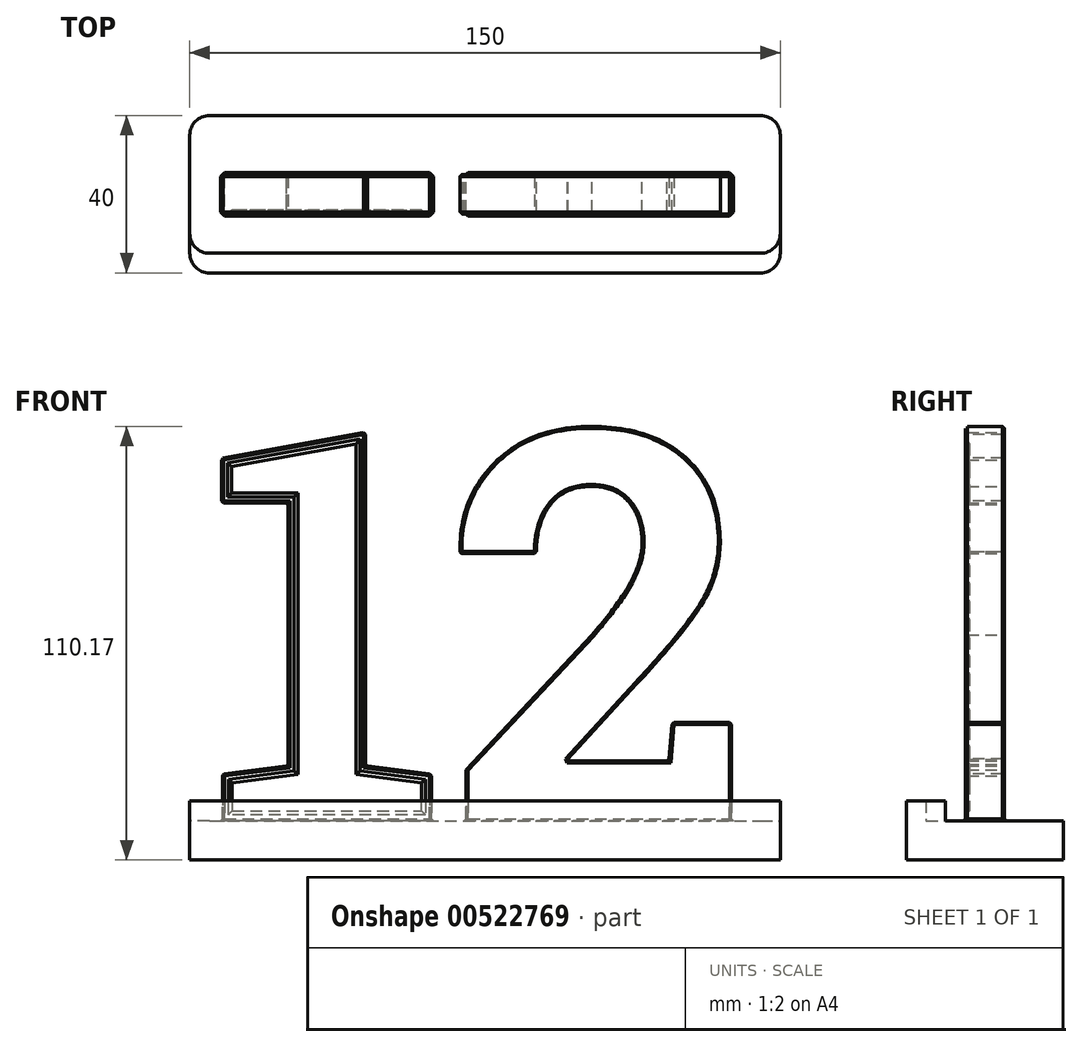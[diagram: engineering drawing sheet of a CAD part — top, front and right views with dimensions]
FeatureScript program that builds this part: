
annotation { "Feature Type Name" : "Feature", "Feature Type Description" : "" }
export const myFeature = defineFeature(function(context is Context, id is Id, definition is map)
    precondition{}
    {
        {
            var Q0;
            Q0=qCreatedBy(makeId("Front.planeOp"),FACE);
            var sketch = newSketch(context, id + "F0", { "sketchPlane" : qUnion([Q0])});
            skText(sketch, "E0", { "text": "12", "fontName": "RobotoSlab-Bold.ttf"});
            const initialGuessF0  = {"E0": [-0.07112, 0, 1, 0, 0.1]};
            skSetInitialGuess(sketch, initialGuessF0);
            skSolve(sketch);
        }
        {
            var Q0;
            Q0=makeQuery(id+"F0.imprint","IMPRINT",FACE,{"disambiguationData":[TD([[makeQuery(id+"F0.imprint","IMPRINT",EDGE,{"derivedFrom":sQuery(id+"F0.wireOp",EDGE,"E0.sketch_text.stroke-0")}),-1.0]])]});
            var Q1;
            Q1=makeQuery(id+"F0.imprint","IMPRINT",FACE,{"disambiguationData":[TD([[makeQuery(id+"F0.imprint","IMPRINT",EDGE,{"derivedFrom":sQuery(id+"F0.wireOp",EDGE,"E0.sketch_text.stroke-10")}),-1.0]])]});
            extrude(context, id + "F1", {"entities" : qUnion([Q0, Q1]), "depth" : 5 * mm, "offsetDistance" : 25 * mm, "hasSecondDirection" : true, "secondDirectionOppositeDirection" : true, "secondDirectionDepth" : 5 * mm});
        }
        {
            var Q0;
            Q0=qCreatedBy(makeId("Front.planeOp"),FACE);
            var sketch = newSketch(context, id + "F2", { "sketchPlane" : qUnion([Q0])});
            skLineSegment(sketch, "E1.bottom", {"start": v(-75, -10) * mm, "end": v(75, -10) * mm});
            skLineSegment(sketch, "E1.top", {"start": v(-75, 0) * mm, "end": v(75, 0) * mm});
            skLineSegment(sketch, "E1.left", {"start": v(-75, -10) * mm, "end": v(-75, 0) * mm});
            skLineSegment(sketch, "E1.right", {"start": v(75, -10) * mm, "end": v(75, 0) * mm});
            skSolve(sketch);
        }
        {
            var Q0;
            Q0=makeQuery(id+"F2.imprint","IMPRINT",FACE,{"disambiguationData":[TD([[makeQuery(id+"F2.imprint","IMPRINT",EDGE,{"derivedFrom":sQuery(id+"F2.wireOp",EDGE,"E1.bottom")}),1.0]])]});
            extrude(context, id + "F3", {"entities" : qUnion([Q0]), "operationType" : NewBodyOperationType.ADD, "depth" : 20 * mm, "offsetDistance" : 25 * mm, "hasSecondDirection" : true, "secondDirectionOppositeDirection" : true, "secondDirectionDepth" : 20 * mm});
        }
        {
            var Q0;
            Q0=makeQuery(id+"F1.opExtrude","CAP_FACE",FACE,{"disambiguationData":[OSD([sQuery(id+"F0.wireOp",EDGE,"E0.sketch_text.stroke-0"),sQuery(id+"F0.wireOp",EDGE,"E0.sketch_text.stroke-1"),sQuery(id+"F0.wireOp",EDGE,"E0.sketch_text.stroke-2"),sQuery(id+"F0.wireOp",EDGE,"E0.sketch_text.stroke-3"),sQuery(id+"F0.wireOp",EDGE,"E0.sketch_text.stroke-4"),sQuery(id+"F0.wireOp",EDGE,"E0.sketch_text.stroke-5"),sQuery(id+"F0.wireOp",EDGE,"E0.sketch_text.stroke-6"),sQuery(id+"F0.wireOp",EDGE,"E0.sketch_text.stroke-7"),sQuery(id+"F0.wireOp",EDGE,"E0.sketch_text.stroke-8"),sQuery(id+"F0.wireOp",EDGE,"E0.sketch_text.stroke-9")])],"isStart":false});
            var sketch = newSketch(context, id + "F4", { "sketchPlane" : qUnion([Q0])});
            skLineSegment(sketch, "E2.0", {"start": v(-48.02, 12.14) * mm, "end": v(-64.71, 10.1) * mm});
            skLineSegment(sketch, "E2.1", {"start": v(-48.02, 82.77) * mm, "end": v(-48.02, 12.14) * mm});
            skLineSegment(sketch, "E2.2", {"start": v(-64.71, 10.1) * mm, "end": v(-64.71, 2) * mm});
            skLineSegment(sketch, "E2.3", {"start": v(-64.9, 82.77) * mm, "end": v(-48.02, 82.77) * mm});
            skLineSegment(sketch, "E2.4", {"start": v(-64.9, 90.43) * mm, "end": v(-64.9, 82.77) * mm});
            skLineSegment(sketch, "E2.5", {"start": v(-32.3, 96.35) * mm, "end": v(-64.9, 90.43) * mm});
            skLineSegment(sketch, "E2.6", {"start": v(-64.71, 2) * mm, "end": v(-15.6, 2) * mm});
            skLineSegment(sketch, "E2.7", {"start": v(-15.6, 2) * mm, "end": v(-15.6, 10.1) * mm});
            skLineSegment(sketch, "E2.8", {"start": v(-15.6, 10.1) * mm, "end": v(-32.3, 12.14) * mm});
            skLineSegment(sketch, "E2.9", {"start": v(-32.3, 12.14) * mm, "end": v(-32.3, 96.35) * mm});
            skFitSpline(sketch, "E3.0", {"points": [v(15.01, 81.48) * mm, v(13.83, 79.93) * mm, v(12, 76.41) * mm, v(11.24, 72.17) * mm, v(11.1, 69.88) * mm]});
            skFitSpline(sketch, "E3.1", {"points": [v(27.02, 86.92) * mm, v(25.76, 86.92) * mm, v(23.36, 86.7) * mm, v(20.1, 85.7) * mm, v(17.26, 83.98) * mm, v(15.7, 82.38) * mm, v(15.01, 81.48) * mm]});
            skFitSpline(sketch, "E3.2", {"points": [v(38.07, 82.24) * mm, v(37.41, 83.02) * mm, v(35.94, 84.4) * mm, v(33.3, 85.87) * mm, v(30.33, 86.74) * mm, v(28.15, 86.92) * mm, v(27.02, 86.92) * mm]});
            skFitSpline(sketch, "E3.3", {"points": [v(41.9, 70.72) * mm, v(41.9, 71.86) * mm, v(41.76, 74.04) * mm, v(41.05, 77.08) * mm, v(39.85, 79.84) * mm, v(38.72, 81.48) * mm, v(38.07, 82.24) * mm]});
            skFitSpline(sketch, "E3.4", {"points": [v(38.75, 59.66) * mm, v(39.78, 61.58) * mm, v(41.36, 65.34) * mm, v(41.9, 68.96) * mm, v(41.9, 70.72) * mm]});
            skLineSegment(sketch, "E3.5", {"start": v(11.1, 69.88) * mm, "end": v(-4.36, 69.88) * mm});
            skFitSpline(sketch, "E3.6", {"points": [v(28.66, 45.89) * mm, v(31, 48.57) * mm, v(35, 53.53) * mm, v(37.72, 57.73) * mm, v(38.75, 59.66) * mm]});
            skLineSegment(sketch, "E3.7", {"start": v(-2.8, 12.17) * mm, "end": v(28.63, 45.86) * mm});
            skLineSegment(sketch, "E3.8", {"start": v(-2.8, 2) * mm, "end": v(-2.8, 12.17) * mm});
            skLineSegment(sketch, "E3.9", {"start": v(60.6, 2) * mm, "end": v(-2.8, 2) * mm});
            skLineSegment(sketch, "E3.10", {"start": v(60.6, 22.96) * mm, "end": v(60.6, 2) * mm});
            skLineSegment(sketch, "E3.11", {"start": v(49.4, 22.96) * mm, "end": v(60.6, 22.96) * mm});
            skFitSpline(sketch, "E3.12", {"points": [v(49.68, 90.75) * mm, v(51.03, 89.52) * mm, v(53.38, 86.87) * mm, v(55.9, 82.31) * mm, v(57.42, 77.1) * mm, v(57.77, 73.16) * mm, v(57.77, 71.07) * mm]});
            skFitSpline(sketch, "E3.13", {"points": [v(27.02, 98.17) * mm, v(29.47, 98.17) * mm, v(34.1, 97.85) * mm, v(40.16, 96.44) * mm, v(45.38, 94.12) * mm, v(48.32, 91.98) * mm, v(49.68, 90.75) * mm]});
            skFitSpline(sketch, "E3.14", {"points": [v(3.86, 89.51) * mm, v(5.28, 90.96) * mm, v(8.35, 93.47) * mm, v(13.7, 96.16) * mm, v(19.87, 97.8) * mm, v(24.54, 98.17) * mm, v(27.02, 98.17) * mm]});
            skFitSpline(sketch, "E3.15", {"points": [v(-4.36, 68.34) * mm, v(-4.41, 70.45) * mm, v(-4.14, 74.49) * mm, v(-2.64, 80) * mm, v(-0.05, 85) * mm, v(2.42, 88.06) * mm, v(3.86, 89.51) * mm]});
            skFitSpline(sketch, "E3.16", {"points": [v(57.77, 71.07) * mm, v(57.77, 68.27) * mm, v(57, 62.94) * mm, v(54.71, 58) * mm, v(53.17, 55.62) * mm]});
            skFitSpline(sketch, "E3.17", {"points": [v(53.17, 55.62) * mm, v(51.6, 53.18) * mm, v(47.32, 47.45) * mm, v(40.86, 40.14) * mm, v(37.08, 36.09) * mm]});
            skLineSegment(sketch, "E3.18", {"start": v(37.07, 36.08) * mm, "end": v(18.68, 15.98) * mm});
            skLineSegment(sketch, "E3.19", {"start": v(18.68, 15.98) * mm, "end": v(19.73, 13.2) * mm});
            skLineSegment(sketch, "E3.20", {"start": v(19.73, 13.2) * mm, "end": v(48.58, 13.2) * mm});
            skLineSegment(sketch, "E3.21", {"start": v(48.58, 13.2) * mm, "end": v(49.4, 22.96) * mm});
            skLineSegment(sketch, "E4", {"start": v(28.63, 45.86) * mm, "end": v(28.66, 45.89) * mm});
            skLineSegment(sketch, "E5", {"start": v(37.07, 36.08) * mm, "end": v(37.08, 36.09) * mm});
            skSolve(sketch);
        }
        {
            var Q0;
            Q0=makeQuery(id+"F4.imprint","IMPRINT",FACE,{"disambiguationData":[TD([[makeQuery(id+"F4.imprint","IMPRINT",EDGE,{"derivedFrom":sQuery(id+"F4.wireOp",EDGE,"E2.0")}),1.0]])]});
            var Q1;
            Q1=makeQuery(id+"F4.imprint","IMPRINT",FACE,{"disambiguationData":[TD([[makeQuery(id+"F4.imprint","IMPRINT",EDGE,{"derivedFrom":sQuery(id+"F4.wireOp",EDGE,"E3.0")}),-1.0]])]});
            extrude(context, id + "F5", {"entities" : qUnion([Q0, Q1]), "operationType" : NewBodyOperationType.REMOVE, "oppositeDirection" : true, "depth" : 1 * mm, "offsetDistance" : 25 * mm});
        }
        {
            var Q0;
            Q0=makeQuery(id+"F1.opExtrude","CAP_FACE",FACE,{"disambiguationData":[OSD([sQuery(id+"F0.wireOp",EDGE,"E0.sketch_text.stroke-10"),sQuery(id+"F0.wireOp",EDGE,"E0.sketch_text.stroke-11"),sQuery(id+"F0.wireOp",EDGE,"E0.sketch_text.stroke-12"),sQuery(id+"F0.wireOp",EDGE,"E0.sketch_text.stroke-13"),sQuery(id+"F0.wireOp",EDGE,"E0.sketch_text.stroke-14"),sQuery(id+"F0.wireOp",EDGE,"E0.sketch_text.stroke-15"),sQuery(id+"F0.wireOp",EDGE,"E0.sketch_text.stroke-16"),sQuery(id+"F0.wireOp",EDGE,"E0.sketch_text.stroke-17"),sQuery(id+"F0.wireOp",EDGE,"E0.sketch_text.stroke-18"),sQuery(id+"F0.wireOp",EDGE,"E0.sketch_text.stroke-19"),sQuery(id+"F0.wireOp",EDGE,"E0.sketch_text.stroke-20"),sQuery(id+"F0.wireOp",EDGE,"E0.sketch_text.stroke-21"),sQuery(id+"F0.wireOp",EDGE,"E0.sketch_text.stroke-22"),sQuery(id+"F0.wireOp",EDGE,"E0.sketch_text.stroke-23"),sQuery(id+"F0.wireOp",EDGE,"E0.sketch_text.stroke-24"),sQuery(id+"F0.wireOp",EDGE,"E0.sketch_text.stroke-25"),sQuery(id+"F0.wireOp",EDGE,"E0.sketch_text.stroke-26"),sQuery(id+"F0.wireOp",EDGE,"E0.sketch_text.stroke-27"),sQuery(id+"F0.wireOp",EDGE,"E0.sketch_text.stroke-28"),sQuery(id+"F0.wireOp",EDGE,"E0.sketch_text.stroke-29"),sQuery(id+"F0.wireOp",EDGE,"E0.sketch_text.stroke-30"),sQuery(id+"F0.wireOp",EDGE,"E0.sketch_text.stroke-31"),sQuery(id+"F0.wireOp",EDGE,"E0.sketch_text.stroke-32")])],"isStart":false});
            var Q1;
            Q1=makeQuery(id+"F1.opExtrude","CAP_FACE",FACE,{"disambiguationData":[OSD([sQuery(id+"F0.wireOp",EDGE,"E0.sketch_text.stroke-0"),sQuery(id+"F0.wireOp",EDGE,"E0.sketch_text.stroke-1"),sQuery(id+"F0.wireOp",EDGE,"E0.sketch_text.stroke-2"),sQuery(id+"F0.wireOp",EDGE,"E0.sketch_text.stroke-3"),sQuery(id+"F0.wireOp",EDGE,"E0.sketch_text.stroke-4"),sQuery(id+"F0.wireOp",EDGE,"E0.sketch_text.stroke-5"),sQuery(id+"F0.wireOp",EDGE,"E0.sketch_text.stroke-6"),sQuery(id+"F0.wireOp",EDGE,"E0.sketch_text.stroke-7"),sQuery(id+"F0.wireOp",EDGE,"E0.sketch_text.stroke-8"),sQuery(id+"F0.wireOp",EDGE,"E0.sketch_text.stroke-9")])],"isStart":false});
            var Q2;
            Q2=makeQuery(id+"F1.opExtrude","CAP_FACE",FACE,{"disambiguationData":[OSD([sQuery(id+"F0.wireOp",EDGE,"E0.sketch_text.stroke-0"),sQuery(id+"F0.wireOp",EDGE,"E0.sketch_text.stroke-1"),sQuery(id+"F0.wireOp",EDGE,"E0.sketch_text.stroke-2"),sQuery(id+"F0.wireOp",EDGE,"E0.sketch_text.stroke-3"),sQuery(id+"F0.wireOp",EDGE,"E0.sketch_text.stroke-4"),sQuery(id+"F0.wireOp",EDGE,"E0.sketch_text.stroke-5"),sQuery(id+"F0.wireOp",EDGE,"E0.sketch_text.stroke-6"),sQuery(id+"F0.wireOp",EDGE,"E0.sketch_text.stroke-7"),sQuery(id+"F0.wireOp",EDGE,"E0.sketch_text.stroke-8"),sQuery(id+"F0.wireOp",EDGE,"E0.sketch_text.stroke-9")])],"isStart":true});
            var Q3;
            Q3=makeQuery(id+"F1.opExtrude","CAP_FACE",FACE,{"disambiguationData":[OSD([sQuery(id+"F0.wireOp",EDGE,"E0.sketch_text.stroke-10"),sQuery(id+"F0.wireOp",EDGE,"E0.sketch_text.stroke-11"),sQuery(id+"F0.wireOp",EDGE,"E0.sketch_text.stroke-12"),sQuery(id+"F0.wireOp",EDGE,"E0.sketch_text.stroke-13"),sQuery(id+"F0.wireOp",EDGE,"E0.sketch_text.stroke-14"),sQuery(id+"F0.wireOp",EDGE,"E0.sketch_text.stroke-15"),sQuery(id+"F0.wireOp",EDGE,"E0.sketch_text.stroke-16"),sQuery(id+"F0.wireOp",EDGE,"E0.sketch_text.stroke-17"),sQuery(id+"F0.wireOp",EDGE,"E0.sketch_text.stroke-18"),sQuery(id+"F0.wireOp",EDGE,"E0.sketch_text.stroke-19"),sQuery(id+"F0.wireOp",EDGE,"E0.sketch_text.stroke-20"),sQuery(id+"F0.wireOp",EDGE,"E0.sketch_text.stroke-21"),sQuery(id+"F0.wireOp",EDGE,"E0.sketch_text.stroke-22"),sQuery(id+"F0.wireOp",EDGE,"E0.sketch_text.stroke-23"),sQuery(id+"F0.wireOp",EDGE,"E0.sketch_text.stroke-24"),sQuery(id+"F0.wireOp",EDGE,"E0.sketch_text.stroke-25"),sQuery(id+"F0.wireOp",EDGE,"E0.sketch_text.stroke-26"),sQuery(id+"F0.wireOp",EDGE,"E0.sketch_text.stroke-27"),sQuery(id+"F0.wireOp",EDGE,"E0.sketch_text.stroke-28"),sQuery(id+"F0.wireOp",EDGE,"E0.sketch_text.stroke-29"),sQuery(id+"F0.wireOp",EDGE,"E0.sketch_text.stroke-30"),sQuery(id+"F0.wireOp",EDGE,"E0.sketch_text.stroke-31"),sQuery(id+"F0.wireOp",EDGE,"E0.sketch_text.stroke-32")])],"isStart":true});
            chamfer(context, id + "F6", {"entities" : qUnion([Q0, Q1, Q2, Q3]), "width" : .5 * mm, "tangentPropagation" : true});
        }
        {
            var Q0;
            Q0=makeQuery(id+"FXvaEfMhF3I8DCv_1.1.F5.boolean.opBoolean","COPY",FACE,{"derivedFrom":makeQuery(id+"FXvaEfMhF3I8DCv_1.1.F5.opExtrude","CAP_FACE",FACE,{"disambiguationData":[OSD([sQuery(id+"F4.wireOp",EDGE,"E3.0"),sQuery(id+"F4.wireOp",EDGE,"E3.1"),sQuery(id+"F4.wireOp",EDGE,"E3.2"),sQuery(id+"F4.wireOp",EDGE,"E3.3"),sQuery(id+"F4.wireOp",EDGE,"E3.4"),sQuery(id+"F4.wireOp",EDGE,"E3.5"),sQuery(id+"F4.wireOp",EDGE,"E3.6"),sQuery(id+"F4.wireOp",EDGE,"E3.7"),sQuery(id+"F4.wireOp",EDGE,"E3.8"),sQuery(id+"F4.wireOp",EDGE,"E3.9"),sQuery(id+"F4.wireOp",EDGE,"E3.10"),sQuery(id+"F4.wireOp",EDGE,"E3.11"),sQuery(id+"F4.wireOp",EDGE,"E3.12"),sQuery(id+"F4.wireOp",EDGE,"E3.13"),sQuery(id+"F4.wireOp",EDGE,"E3.14"),sQuery(id+"F4.wireOp",EDGE,"E3.15"),sQuery(id+"F4.wireOp",EDGE,"E3.16"),sQuery(id+"F4.wireOp",EDGE,"E3.17"),sQuery(id+"F4.wireOp",EDGE,"E3.18"),sQuery(id+"F4.wireOp",EDGE,"E3.19"),sQuery(id+"F4.wireOp",EDGE,"E3.20"),sQuery(id+"F4.wireOp",EDGE,"E3.21"),sQuery(id+"F4.wireOp",EDGE,"E4"),sQuery(id+"F4.wireOp",EDGE,"E5")])],"isStart":false})});
            var Q1;
            Q1=makeQuery(id+"FXvaEfMhF3I8DCv_1.1.F5.boolean.opBoolean","COPY",FACE,{"derivedFrom":makeQuery(id+"FXvaEfMhF3I8DCv_1.1.F5.opExtrude","CAP_FACE",FACE,{"disambiguationData":[OSD([sQuery(id+"F4.wireOp",EDGE,"E2.0"),sQuery(id+"F4.wireOp",EDGE,"E2.1"),sQuery(id+"F4.wireOp",EDGE,"E2.2"),sQuery(id+"F4.wireOp",EDGE,"E2.3"),sQuery(id+"F4.wireOp",EDGE,"E2.4"),sQuery(id+"F4.wireOp",EDGE,"E2.5"),sQuery(id+"F4.wireOp",EDGE,"E2.6"),sQuery(id+"F4.wireOp",EDGE,"E2.7"),sQuery(id+"F4.wireOp",EDGE,"E2.8"),sQuery(id+"F4.wireOp",EDGE,"E2.9")])],"isStart":false})});
            var Q2;
            Q2=makeQuery(id+"F5.boolean.opBoolean","COPY",FACE,{"derivedFrom":makeQuery(id+"F5.opExtrude","CAP_FACE",FACE,{"disambiguationData":[OSD([sQuery(id+"F4.wireOp",EDGE,"E2.0"),sQuery(id+"F4.wireOp",EDGE,"E2.1"),sQuery(id+"F4.wireOp",EDGE,"E2.2"),sQuery(id+"F4.wireOp",EDGE,"E2.3"),sQuery(id+"F4.wireOp",EDGE,"E2.4"),sQuery(id+"F4.wireOp",EDGE,"E2.5"),sQuery(id+"F4.wireOp",EDGE,"E2.6"),sQuery(id+"F4.wireOp",EDGE,"E2.7"),sQuery(id+"F4.wireOp",EDGE,"E2.8"),sQuery(id+"F4.wireOp",EDGE,"E2.9")])],"isStart":false})});
            var Q3;
            Q3=makeQuery(id+"F5.boolean.opBoolean","COPY",FACE,{"derivedFrom":makeQuery(id+"F5.opExtrude","CAP_FACE",FACE,{"disambiguationData":[OSD([sQuery(id+"F4.wireOp",EDGE,"E3.0"),sQuery(id+"F4.wireOp",EDGE,"E3.1"),sQuery(id+"F4.wireOp",EDGE,"E3.2"),sQuery(id+"F4.wireOp",EDGE,"E3.3"),sQuery(id+"F4.wireOp",EDGE,"E3.4"),sQuery(id+"F4.wireOp",EDGE,"E3.5"),sQuery(id+"F4.wireOp",EDGE,"E3.6"),sQuery(id+"F4.wireOp",EDGE,"E3.7"),sQuery(id+"F4.wireOp",EDGE,"E3.8"),sQuery(id+"F4.wireOp",EDGE,"E3.9"),sQuery(id+"F4.wireOp",EDGE,"E3.10"),sQuery(id+"F4.wireOp",EDGE,"E3.11"),sQuery(id+"F4.wireOp",EDGE,"E3.12"),sQuery(id+"F4.wireOp",EDGE,"E3.13"),sQuery(id+"F4.wireOp",EDGE,"E3.14"),sQuery(id+"F4.wireOp",EDGE,"E3.15"),sQuery(id+"F4.wireOp",EDGE,"E3.16"),sQuery(id+"F4.wireOp",EDGE,"E3.17"),sQuery(id+"F4.wireOp",EDGE,"E3.18"),sQuery(id+"F4.wireOp",EDGE,"E3.19"),sQuery(id+"F4.wireOp",EDGE,"E3.20"),sQuery(id+"F4.wireOp",EDGE,"E3.21"),sQuery(id+"F4.wireOp",EDGE,"E4"),sQuery(id+"F4.wireOp",EDGE,"E5")])],"isStart":false})});
            chamfer(context, id + "F7", {"entities" : qUnion([Q0, Q1, Q2, Q3]), "width" : .5 * mm, "tangentPropagation" : true});
        }
        {
            var Q0;
            Q0=makeQuery(id+"F3.opExtrude","CAP_EDGE",EDGE,{"disambiguationData":[OSD([sQuery(id+"F2.wireOp",EDGE,"E1.left")])],"isStart":false});
            var Q1;
            Q1=makeQuery(id+"F3.opExtrude","CAP_EDGE",EDGE,{"disambiguationData":[OSD([sQuery(id+"F2.wireOp",EDGE,"E1.left")])],"isStart":true});
            var Q2;
            Q2=makeQuery(id+"F3.opExtrude","CAP_EDGE",EDGE,{"disambiguationData":[OSD([sQuery(id+"F2.wireOp",EDGE,"E1.right")])],"isStart":false});
            var Q3;
            Q3=makeQuery(id+"F3.opExtrude","CAP_EDGE",EDGE,{"disambiguationData":[OSD([sQuery(id+"F2.wireOp",EDGE,"E1.right")])],"isStart":true});
            fillet(context, id + "F8", {"entities" : qUnion([Q0, Q1, Q2, Q3]), "radius" : 5 * mm, "tangentPropagation" : true, "allowEdgeOverflow" : false});
        }
        {
            var Q0;
            Q0=makeQuery(id+"F1.opExtrude","SWEPT_EDGE",EDGE,{"disambiguationData":[OSD([sQuery(id+"F0.wireOp",EDGE,"E0.sketch_text.stroke-0"),sQuery(id+"F0.wireOp",EDGE,"E0.sketch_text.stroke-9")])]});
            var Q1;
            Q1=makeQuery(id+"F1.opExtrude","SWEPT_EDGE",EDGE,{"disambiguationData":[OSD([sQuery(id+"F0.wireOp",EDGE,"E0.sketch_text.stroke-0"),sQuery(id+"F0.wireOp",EDGE,"E0.sketch_text.stroke-1")])]});
            var Q2;
            Q2=makeQuery(id+"F1.opExtrude","SWEPT_EDGE",EDGE,{"disambiguationData":[OSD([sQuery(id+"F0.wireOp",EDGE,"E0.sketch_text.stroke-5"),sQuery(id+"F0.wireOp",EDGE,"E0.sketch_text.stroke-6")])]});
            var Q3;
            Q3=makeQuery(id+"F1.opExtrude","SWEPT_EDGE",EDGE,{"disambiguationData":[OSD([sQuery(id+"F0.wireOp",EDGE,"E0.sketch_text.stroke-6"),sQuery(id+"F0.wireOp",EDGE,"E0.sketch_text.stroke-7")])]});
            var Q4;
            Q4=makeQuery(id+"F1.opExtrude","SWEPT_EDGE",EDGE,{"disambiguationData":[OSD([sQuery(id+"F0.wireOp",EDGE,"E0.sketch_text.stroke-4"),sQuery(id+"F0.wireOp",EDGE,"E0.sketch_text.stroke-5")])]});
            var Q5;
            Q5=makeQuery(id+"F1.opExtrude","SWEPT_EDGE",EDGE,{"disambiguationData":[OSD([sQuery(id+"F0.wireOp",EDGE,"E0.sketch_text.stroke-3"),sQuery(id+"F0.wireOp",EDGE,"E0.sketch_text.stroke-4")])]});
            var Q6;
            Q6=makeQuery(id+"F1.opExtrude","SWEPT_EDGE",EDGE,{"disambiguationData":[OSD([sQuery(id+"F0.wireOp",EDGE,"E0.sketch_text.stroke-2"),sQuery(id+"F0.wireOp",EDGE,"E0.sketch_text.stroke-3")])]});
            var Q7;
            Q7=makeQuery(id+"F1.opExtrude","SWEPT_EDGE",EDGE,{"disambiguationData":[OSD([sQuery(id+"F0.wireOp",EDGE,"E0.sketch_text.stroke-1"),sQuery(id+"F0.wireOp",EDGE,"E0.sketch_text.stroke-2")])]});
            var Q8;
            Q8=makeQuery(id+"F1.opExtrude","SWEPT_EDGE",EDGE,{"disambiguationData":[OSD([sQuery(id+"F0.wireOp",EDGE,"E0.sketch_text.stroke-18"),sQuery(id+"F0.wireOp",EDGE,"E0.sketch_text.stroke-19")])]});
            var Q9;
            Q9=makeQuery(id+"F1.opExtrude","SWEPT_EDGE",EDGE,{"disambiguationData":[OSD([sQuery(id+"F0.wireOp",EDGE,"E0.sketch_text.stroke-17"),sQuery(id+"F0.wireOp",EDGE,"E0.sketch_text.stroke-18")])]});
            var Q10;
            Q10=makeQuery(id+"F1.opExtrude","SWEPT_EDGE",EDGE,{"disambiguationData":[OSD([sQuery(id+"F0.wireOp",EDGE,"E0.sketch_text.stroke-29"),sQuery(id+"F0.wireOp",EDGE,"E0.sketch_text.stroke-30")])]});
            var Q11;
            Q11=makeQuery(id+"F1.opExtrude","SWEPT_EDGE",EDGE,{"disambiguationData":[OSD([sQuery(id+"F0.wireOp",EDGE,"E0.sketch_text.stroke-30"),sQuery(id+"F0.wireOp",EDGE,"E0.sketch_text.stroke-31")])]});
            var Q12;
            Q12=makeQuery(id+"F1.opExtrude","SWEPT_EDGE",EDGE,{"disambiguationData":[OSD([sQuery(id+"F0.wireOp",EDGE,"E0.sketch_text.stroke-28"),sQuery(id+"F0.wireOp",EDGE,"E0.sketch_text.stroke-29")])]});
            chamfer(context, id + "F9", {"entities" : qUnion([Q0, Q1, Q2, Q3, Q4, Q5, Q6, Q7, Q8, Q9, Q10, Q11, Q12]), "width" : .5 * mm, "tangentPropagation" : true});
        }
        {
            var Q0;
            Q0=makeQuery(id+"F3.opExtrude","SWEPT_FACE",FACE,{"disambiguationData":[OSD([sQuery(id+"F2.wireOp",EDGE,"E1.top")])]});
            var sketch = newSketch(context, id + "F10", { "sketchPlane" : qUnion([Q0])});
            skLineSegment(sketch, "E6", {"start": v(-70, -15) * mm, "end": v(70, -15) * mm});
            skArc(sketch, "E7", {"start": v(70, -15) * mm, "mid": v(73.54, -13.54) * mm, "end": v(75, -10) * mm});
            skArc(sketch, "E8", {"start": v(-75, -10) * mm, "mid": v(-73.54, -13.54) * mm, "end": v(-70, -15) * mm});
            skSolve(sketch);
        }
        {
            var Q0;
            Q0=makeQuery(id+"F10.imprint","IMPRINT",FACE,{"disambiguationData":[TD([[makeQuery(id+"F10.imprint","IMPRINT",EDGE,{"derivedFrom":sQuery(id+"F10.wireOp",EDGE,"E6")}),-1.0]])]});
            extrude(context, id + "F11", {"entities" : qUnion([Q0]), "operationType" : NewBodyOperationType.ADD, "depth" : 5 * mm, "offsetDistance" : 25 * mm});
        }
    });
